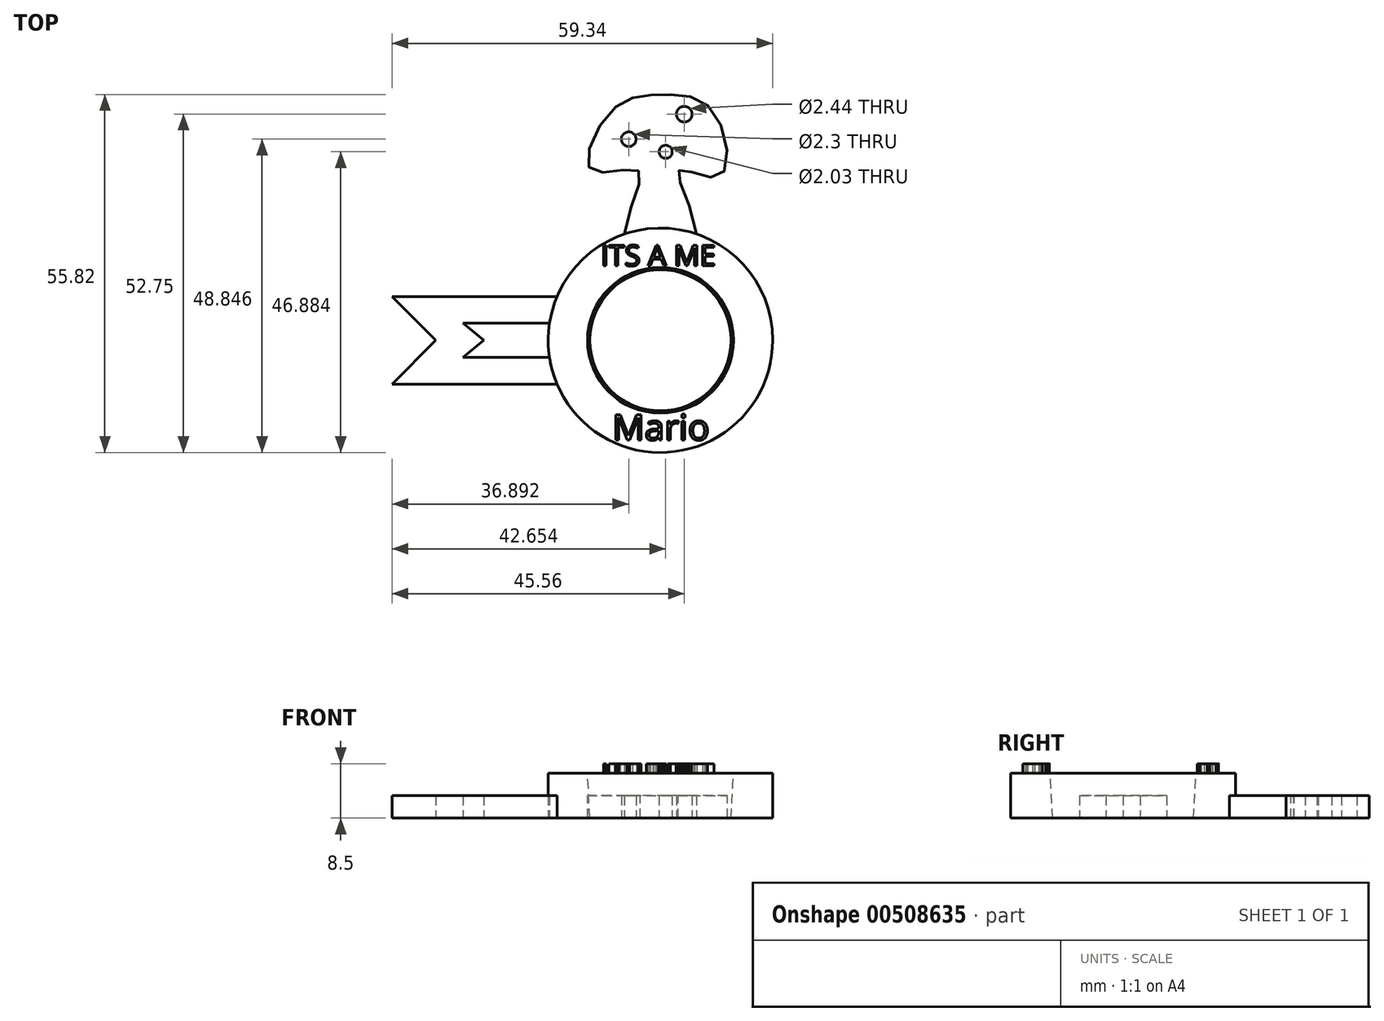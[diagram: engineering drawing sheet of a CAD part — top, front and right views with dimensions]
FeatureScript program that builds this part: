
annotation { "Feature Type Name" : "Feature", "Feature Type Description" : "" }
export const myFeature = defineFeature(function(context is Context, id is Id, definition is map)
    precondition{}
    {
        {
            var Q0;
            Q0=qCreatedBy(makeId("Top.planeOp"),FACE);
            var sketch = newSketch(context, id + "F0", { "sketchPlane" : qUnion([Q0])});
            skCircle(sketch, "E0", {"center": v(0, 0) * mm, "radius": 17.5 * mm});
            skCircle(sketch, "E1", {"center": v(0, 0) * mm, "radius": 11 * mm});
            skFitSpline(sketch, "E2", {"points": [v(-5.65, 16.56) * mm, v(-3.54, 26.5) * mm, v(-10.75, 26.52) * mm, v(-7.64, 35.75) * mm, v(0, 38.3) * mm, v(8.16, 35.76) * mm, v(9.22, 25.6) * mm, v(3.03, 26.57) * mm, v(5.64, 16.56) * mm], "startDerivative": vector(13.77, 100.89) * mm, "endDerivative": vector(15.07, -105.65) * mm});
            skLineSegment(sketch, "E3", {"start": v(-16.12, -6.82) * mm, "end": v(-41.84, -6.82) * mm});
            skLineSegment(sketch, "E4", {"start": v(-41.84, -6.82) * mm, "end": v(-35.02, 0) * mm});
            skLineSegment(sketch, "E5", {"start": v(-35.02, 0) * mm, "end": v(-41.84, 6.82) * mm});
            skLineSegment(sketch, "E6", {"start": v(-41.84, 6.82) * mm, "end": v(-16.12, 6.82) * mm});
            skLineSegment(sketch, "E7", {"start": v(-17.3, 2.67) * mm, "end": v(-30.79, 2.67) * mm});
            skLineSegment(sketch, "E8", {"start": v(-30.79, 2.67) * mm, "end": v(-27.54, 0) * mm});
            skLineSegment(sketch, "E9", {"start": v(-27.54, 0) * mm, "end": v(-30.79, -2.67) * mm});
            skLineSegment(sketch, "E10", {"start": v(-30.79, -2.67) * mm, "end": v(-17.3, -2.67) * mm});
            skCircle(sketch, "E11", {"center": v(-4.95, 31.35) * mm, "radius": 1.15 * mm});
            skCircle(sketch, "E12", {"center": v(3.72, 35.25) * mm, "radius": 1.22 * mm});
            skCircle(sketch, "E13", {"center": v(0.81, 29.38) * mm, "radius": 1.02 * mm});
            skSolve(sketch);
        }
        {
            var Q0;
            Q0=makeQuery(id+"F0.imprint","IMPRINT",FACE,{"disambiguationData":[TD([[makeQuery(id+"F0.imprint","IMPRINT",EDGE,{"derivedFrom":sQuery(id+"F0.wireOp",EDGE,"E0")}),1.0]])]});
            var Q1;
            Q1=makeQuery(id+"F0.imprint","IMPRINT",FACE,{"disambiguationData":[TD([[makeQuery(id+"F0.imprint","IMPRINT",EDGE,{"derivedFrom":sQuery(id+"F0.wireOp",EDGE,"E1")}),1.0]])]});
            extrude(context, id + "F1", {"entities" : qUnion([Q0, Q1]), "depth" : 7 * mm});
        }
        {
            var Q0;
            Q0=makeQuery(id+"F0.imprint","IMPRINT",FACE,{"disambiguationData":[TD([[makeQuery(id+"F0.imprint","IMPRINT",EDGE,{"derivedFrom":sQuery(id+"F0.wireOp",EDGE,"E1")}),1.0]])]});
            extrude(context, id + "F2", {"entities" : qUnion([Q0]), "operationType" : NewBodyOperationType.REMOVE, "endBound" : BoundingType.THROUGH_ALL, "depth" : 25.4 * mm, "hasDraft" : true, "draftAngle" : 3 * degree});
        }
        {
            var Q0;
            {var subQ0=sQuery(id+"F0.wireOp",EDGE,"E2");Q0=makeQuery(id+"F0.imprint","IMPRINT",FACE,{"disambiguationData":[TD([[makeQuery(id+"F0.imprint","IMPRINT",EDGE,{"derivedFrom":subQ0}),-1.0]])]});}
            var Q1;
            {var subQ0=sQuery(id+"F0.wireOp",EDGE,"E3");Q1=makeQuery(id+"F0.imprint","IMPRINT",FACE,{"disambiguationData":[TD([[makeQuery(id+"F0.imprint","IMPRINT",EDGE,{"derivedFrom":subQ0}),-1.0]])]});}
            extrude(context, id + "F3", {"entities" : qUnion([Q0, Q1]), "operationType" : NewBodyOperationType.ADD, "depth" : 3.5 * mm});
        }
        {
            var Q0;
            Q0=makeQuery(id+"F1.opExtrude","CAP_FACE",FACE,{"disambiguationData":[OSD([sQuery(id+"F0.wireOp",EDGE,"E0")])],"isStart":false});
            var sketch = newSketch(context, id + "F4", { "sketchPlane" : qUnion([Q0])});
            skText(sketch, "E14", { "text": "Mario", "fontName": "OpenSans-Regular.ttf"});
            skText(sketch, "E15", { "text": "ITS A ME", "fontName": "OpenSans-Regular.ttf"});
            const initialGuessF4  = {"E14": [-0.0075, -0.01557, 1, 0, 0.004], "E15": [-0.00933, 0.0116, 1, 0, 0.00324]};
            skSetInitialGuess(sketch, initialGuessF4);
            skSolve(sketch);
        }
        {
            var Q0;
            Q0 = qSketchRegion(id + "F4", true);
            extrude(context, id + "F5", {"entities" : qUnion([Q0]), "operationType" : NewBodyOperationType.ADD, "depth" : 1.5 * mm});
        }
    });
